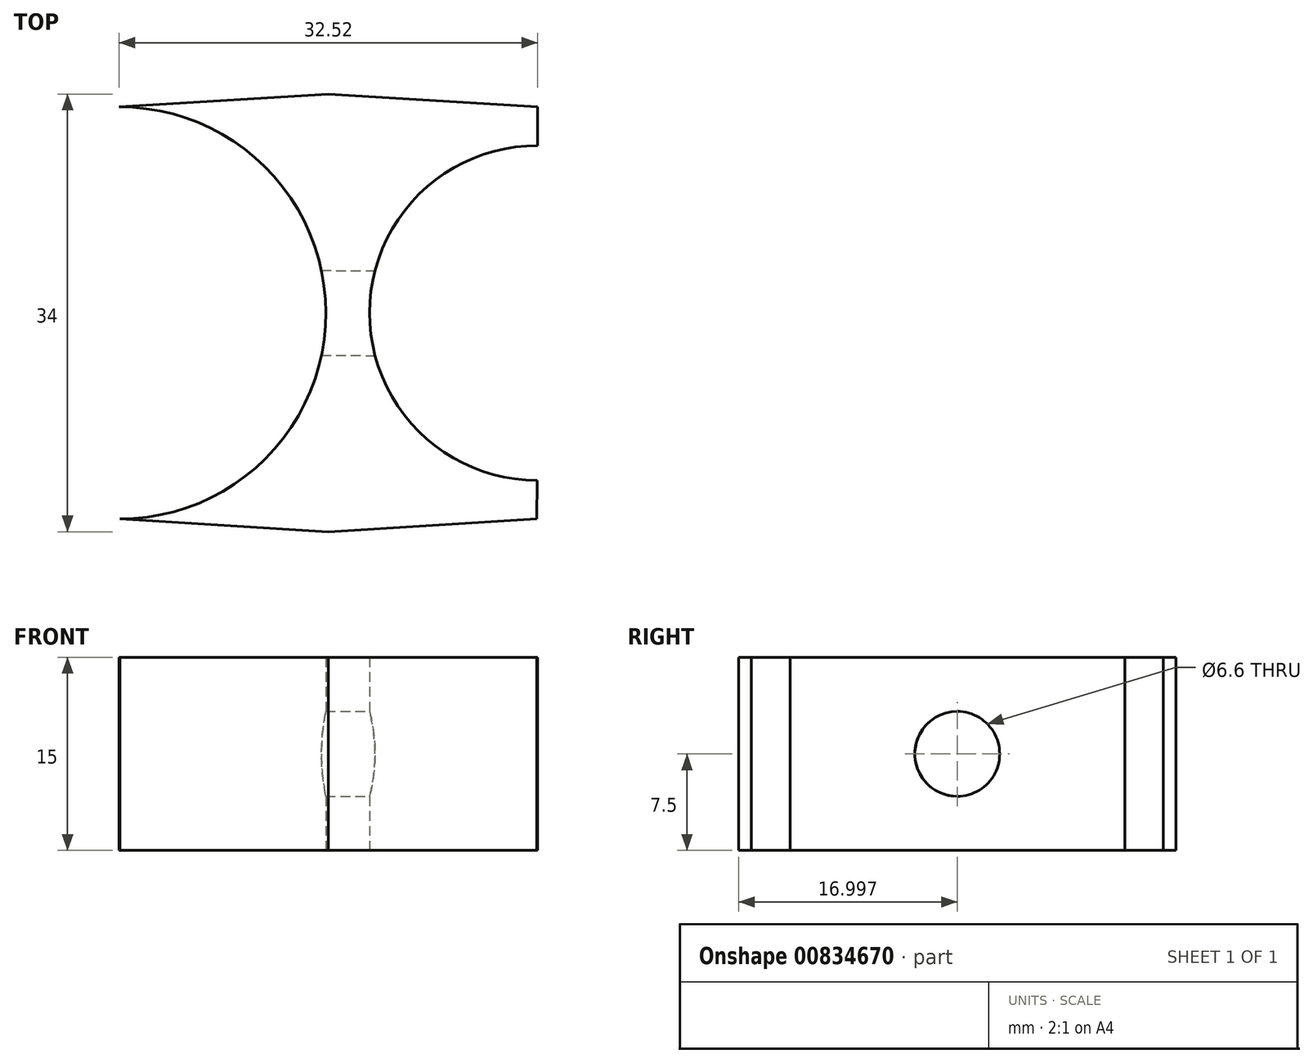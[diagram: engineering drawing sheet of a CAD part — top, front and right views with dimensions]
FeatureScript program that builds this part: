
annotation { "Feature Type Name" : "Feature", "Feature Type Description" : "" }
export const myFeature = defineFeature(function(context is Context, id is Id, definition is map)
    precondition{}
    {
        {
            var Q0;
            Q0=qCreatedBy(makeId("Top.planeOp"),FACE);
            var sketch = newSketch(context, id + "F0", { "sketchPlane" : qUnion([Q0])});
            skArc(sketch, "E0", {"start": v(16.26, 16) * mm, "mid": v(0.2, 0.03) * mm, "end": v(16.2, -16) * mm});
            skArc(sketch, "E1", {"start": v(16.26, 13) * mm, "mid": v(3.2, 0.02) * mm, "end": v(16.2, -13) * mm});
            skLineSegment(sketch, "E2", {"start": v(0, 17) * mm, "end": v(0, -17) * mm});
            skLineSegment(sketch, "E3", {"start": v(0, 17) * mm, "end": v(16.26, 16) * mm});
            skLineSegment(sketch, "E4", {"start": v(0, -17) * mm, "end": v(16.2, -16) * mm});
            skLineSegment(sketch, "E5", {"start": v(16.26, 16) * mm, "end": v(16.2, -16) * mm});
            skLineSegment(sketch, "E6.MirrorCS", {"start": v(0, 17) * mm, "end": v(-16.26, 16) * mm});
            skArc(sketch, "E7.MirrorCS", {"start": v(-16.26, 16) * mm, "mid": v(-0.2, 0.03) * mm, "end": v(-16.2, -16) * mm});
            skLineSegment(sketch, "E8.MirrorCS", {"start": v(0, -17) * mm, "end": v(-16.2, -16) * mm});
            skArc(sketch, "E9.MirrorCS", {"start": v(-16.26, 13) * mm, "mid": v(-3.2, 0.02) * mm, "end": v(-16.2, -13) * mm});
            skLineSegment(sketch, "E10.MirrorCS", {"start": v(-16.26, 16) * mm, "end": v(-16.2, -16) * mm});
            skLineSegment(sketch, "E11", {"start": v(-16.26, 13) * mm, "end": v(-16.2, -13) * mm});
            skLineSegment(sketch, "E12", {"start": v(16.26, 13) * mm, "end": v(16.2, -13) * mm});
            skSolve(sketch);
        }
        {
            var Q0;
            Q0=makeQuery(id+"F0.imprint","IMPRINT",FACE,{"disambiguationData":[TD([[makeQuery(id+"F0.imprint","IMPRINT",EDGE,{"derivedFrom":sQuery(id+"F0.wireOp",EDGE,"E2")}),1.0]])]});
            var Q1;
            Q1=makeQuery(id+"F0.imprint","IMPRINT",FACE,{"disambiguationData":[TD([[makeQuery(id+"F0.imprint","IMPRINT",EDGE,{"derivedFrom":sQuery(id+"F0.wireOp",EDGE,"E1")}),-1.0]])]});
            var Q2;
            Q2=makeQuery(id+"F0.imprint","IMPRINT",FACE,{"disambiguationData":[TD([[makeQuery(id+"F0.imprint","IMPRINT",EDGE,{"derivedFrom":sQuery(id+"F0.wireOp",EDGE,"E1")}),1.0]])]});
            var Q3;
            Q3=makeQuery(id+"F0.imprint","IMPRINT",FACE,{"disambiguationData":[TD([[makeQuery(id+"F0.imprint","IMPRINT",EDGE,{"derivedFrom":sQuery(id+"F0.wireOp",EDGE,"E2")}),-1.0]])]});
            var Q4;
            {var subQ0=sQuery(id+"F0.wireOp",EDGE,"E7.MirrorCS");Q4=makeQuery(id+"F0.imprint","IMPRINT",FACE,{"disambiguationData":[TD([[makeQuery(id+"F0.imprint","IMPRINT",EDGE,{"derivedFrom":subQ0}),-1.0]])]});}
            var Q5;
            {var subQ0=sQuery(id+"F0.wireOp",EDGE,"E9.MirrorCS");Q5=makeQuery(id+"F0.imprint","IMPRINT",FACE,{"disambiguationData":[TD([[makeQuery(id+"F0.imprint","IMPRINT",EDGE,{"derivedFrom":subQ0}),-1.0]])]});}
            extrude(context, id + "F1", {"entities" : qUnion([Q0, Q1, Q2, Q3, Q4, Q5]), "endBound" : BoundingType.SYMMETRIC, "depth" : 15 * mm, "offsetDistance" : 25 * mm});
        }
        {
            var Q0;
            Q0=makeQuery(id+"F0.imprint","IMPRINT",FACE,{"disambiguationData":[TD([[makeQuery(id+"F0.imprint","IMPRINT",EDGE,{"derivedFrom":sQuery(id+"F0.wireOp",EDGE,"E9.MirrorCS")}),-1.0]])]});
            extrude(context, id + "F2", {"entities" : qUnion([Q0]), "operationType" : NewBodyOperationType.REMOVE, "endBound" : BoundingType.SYMMETRIC, "depth" : 25 * mm, "offsetDistance" : 25 * mm});
        }
        {
            var Q0;
            Q0=makeQuery(id+"F0.imprint","IMPRINT",FACE,{"disambiguationData":[TD([[makeQuery(id+"F0.imprint","IMPRINT",EDGE,{"derivedFrom":sQuery(id+"F0.wireOp",EDGE,"E1")}),1.0]])]});
            extrude(context, id + "F3", {"entities" : qUnion([Q0]), "operationType" : NewBodyOperationType.REMOVE, "endBound" : BoundingType.SYMMETRIC, "depth" : 25 * mm, "offsetDistance" : 25 * mm});
        }
        {
            var Q0;
            Q0=makeQuery(id+"F1.opExtrude","SWEPT_FACE",FACE,{"disambiguationData":[OSD([sQuery(id+"F0.wireOp",EDGE,"E5"),sQuery(id+"F0.wireOp",EDGE,"E12")])]});
            var sketch = newSketch(context, id + "F4", { "sketchPlane" : qUnion([Q0])});
            skCircle(sketch, "E13", {"center": v(0, 0) * mm, "radius": 3.3 * mm});
            skCircle(sketch, "E14", {"center": v(0, 0) * mm, "radius": 3.05 * mm});
            skSolve(sketch);
        }
        {
            var Q0;
            Q0=makeQuery(id+"F4.imprint","IMPRINT",FACE,{"disambiguationData":[TD([[makeQuery(id+"F4.imprint","IMPRINT",EDGE,{"derivedFrom":sQuery(id+"F4.wireOp",EDGE,"E13")}),1.0]])]});
            var Q1;
            Q1=makeQuery(id+"F4.imprint","IMPRINT",FACE,{"disambiguationData":[TD([[makeQuery(id+"F4.imprint","IMPRINT",EDGE,{"derivedFrom":sQuery(id+"F4.wireOp",EDGE,"E14")}),1.0]])]});
            extrude(context, id + "F5", {"entities" : qUnion([Q0, Q1]), "operationType" : NewBodyOperationType.REMOVE, "oppositeDirection" : true, "depth" : 25 * mm, "offsetDistance" : 25 * mm});
        }
    });
